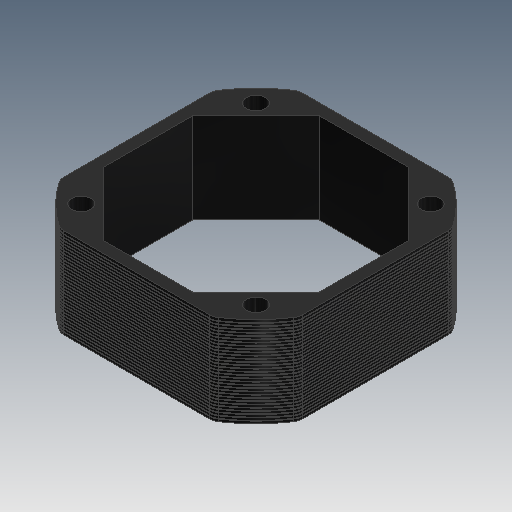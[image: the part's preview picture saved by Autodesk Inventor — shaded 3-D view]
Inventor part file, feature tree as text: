
AUTODESK INVENTOR PART (.ipt)
format: ipt  version: 2020.2 (Build 242310000, 310)  size: 914,944 bytes
history: native  units: mm
features: sketch x3, extrude x2, hole x1, fillet x1, plane x1, pattern_linear x1, projected_geometry x1
ambient origin geometry x8: Origin, YZ Plane, XZ Plane, XY Plane, X Axis, Y Axis, Z Axis, Center Point
bodies: Body1 (feature_tree)
feature tree (10):
  extrude  "Extrusion7"  Depth=42.3mm
  hole  "Hole5"  [1 undecoded]
  fillet  "Fillet8"  Radius=25.125mm
  plane  "Work Plane6"
  extrude  "Extrusion8"  Depth=0.5mm
  pattern_linear  "Rectangular Pattern1"  Spacing1=31.0mm  [1 undecoded]
  sketch  "Sketch11"  dims[d82=42.3mm d83=42.3mm]
  sketch  "Sketch12"  dims[d84=38.3mm d85=50.25mm d86=25.125mm]
  sketch  "Sketch13"  dims[d87=16.0mm d88=0.0mm d89=31.0mm d90=31.0mm d91=3.4mm d92=6.0mm d93=6.3mm d94=2.0mm d95=90.0deg d96=8.0mm d97=20.594885mm d98=2.0mm d99=-0.5mm d100=0.1mm d101=0.1mm d102=0.0mm d103=310.0mm d105=0.5mm]
  projected_geometry  "Projected Loop3"
note: 2 required parameter values undecoded (feature->parameter linkage not recoverable at this tier; creation-order binding heuristic only, values carry confidence <= 0.55)
